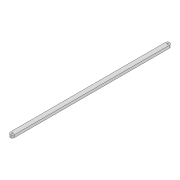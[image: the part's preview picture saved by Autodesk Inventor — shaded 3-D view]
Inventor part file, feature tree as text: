
AUTODESK INVENTOR PART (.ipt)
format: ipt  version: 2022 (Build 260153000, 153)  size: 81,408 bytes
history: native  units: mm
features: extrude x1, sketch x1
ambient origin geometry x8: Origin, YZ Plane, XZ Plane, XY Plane, X Axis, Y Axis, Z Axis, Center Point
bodies: Solid1 (feature_tree)
feature tree (2):
  extrude  "Extrusion1"  Depth=10.0mm
  sketch  "Sketch1"  dims[d1=350.625mm d2=10.0mm d3=3.0mm d4=3.0mm d5=6.0mm d6=0.0mm]
